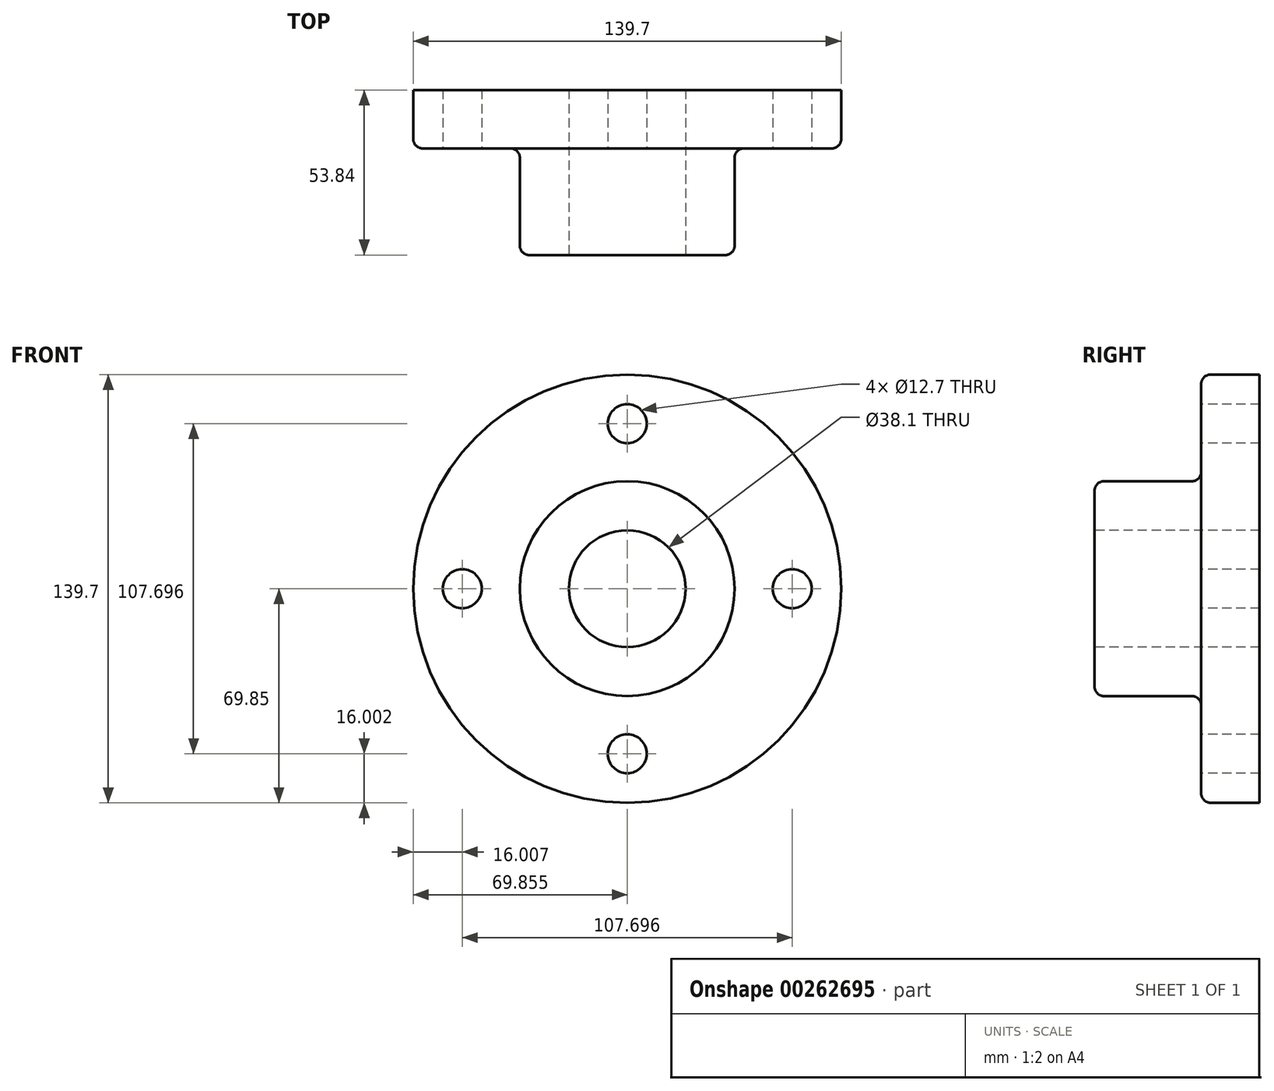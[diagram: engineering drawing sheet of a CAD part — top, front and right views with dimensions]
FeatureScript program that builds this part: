
annotation { "Feature Type Name" : "Feature", "Feature Type Description" : "" }
export const myFeature = defineFeature(function(context is Context, id is Id, definition is map)
    precondition{}
    {
        {
            var Q0;
            Q0=qCreatedBy(makeId("Top.planeOp"),FACE);
            var sketch = newSketch(context, id + "F0", { "sketchPlane" : qUnion([Q0])});
            skLineSegment(sketch, "E0.bottom", {"start": v(-26.3, -57.06) * mm, "end": v(8.75, -57.06) * mm});
            skLineSegment(sketch, "E0.top", {"start": v(-26.3, -3.22) * mm, "end": v(43.54, -3.22) * mm});
            skLineSegment(sketch, "E0.left", {"start": v(-26.3, -57.06) * mm, "end": v(-26.3, -3.22) * mm});
            skLineSegment(sketch, "E0.right", {"start": v(43.54, -22.27) * mm, "end": v(43.54, -3.22) * mm});
            skLineSegment(sketch, "E1.top", {"start": v(43.54, -22.27) * mm, "end": v(8.75, -22.27) * mm});
            skLineSegment(sketch, "E1.right", {"start": v(8.75, -57.06) * mm, "end": v(8.75, -22.27) * mm});
            skSolve(sketch);
        }
        {
            var Q0;
            Q0 = qSketchRegion(id + "F0", true);
            var Q1;
            Q1=sQuery(id+"F0.wireOp",EDGE,"E0.left");
            revolve(context, id + "F1", {"entities" : qUnion([Q0]), "axis" : qUnion([Q1]), "revolveType" : RevolveType.FULL});
        }
        {
            var Q0;
            Q0=makeQuery(id+"F1.opRevolve","SWEPT_FACE",FACE,{"disambiguationData":[OSD([sQuery(id+"F0.wireOp",EDGE,"E1.top")])]});
            var sketch = newSketch(context, id + "F2", { "sketchPlane" : qUnion([Q0])});
            skCircle(sketch, "E2", {"center": v(-26.3, 0) * mm, "radius": 19.05 * mm});
            skSolve(sketch);
        }
        {
            var Q0;
            Q0 = qSketchRegion(id + "F2", true);
            extrude(context, id + "F3", {"entities" : qUnion([Q0]), "operationType" : NewBodyOperationType.REMOVE, "endBound" : BoundingType.SYMMETRIC, "oppositeDirection" : true, "depth" : 101.6 * mm});
        }
        {
            var Q0;
            Q0=makeQuery(id+"F1.opRevolve","SWEPT_FACE",FACE,{"disambiguationData":[OSD([sQuery(id+"F0.wireOp",EDGE,"E1.top")])]});
            var sketch = newSketch(context, id + "F4", { "sketchPlane" : qUnion([Q0])});
            skCircle(sketch, "E3", {"center": v(-80.15, 0) * mm, "radius": 6.35 * mm});
            skCircle(sketch, "E4", {"center": v(27.54, 0) * mm, "radius": 6.35 * mm});
            skCircle(sketch, "E5", {"center": v(-26.3, 53.85) * mm, "radius": 6.35 * mm});
            skCircle(sketch, "E6", {"center": v(-26.3, -53.85) * mm, "radius": 6.35 * mm});
            skPoint(sketch, "E7.center.orphan", {"position": v(-26.3, 0) * mm});
            skSolve(sketch);
        }
        {
            var Q0;
            Q0 = qSketchRegion(id + "F4", true);
            extrude(context, id + "F5", {"entities" : qUnion([Q0]), "operationType" : NewBodyOperationType.REMOVE, "endBound" : BoundingType.SYMMETRIC, "oppositeDirection" : true, "depth" : 101.6 * mm});
        }
        {
            var Q0;
            Q0=makeQuery(id+"F1.opRevolve","SWEPT_EDGE",EDGE,{"disambiguationData":[OSD([sQuery(id+"F0.wireOp",EDGE,"E0.right"),sQuery(id+"F0.wireOp",EDGE,"E1.top")])]});
            var Q1;
            Q1=makeQuery(id+"F1.opRevolve","SWEPT_EDGE",EDGE,{"disambiguationData":[OSD([sQuery(id+"F0.wireOp",EDGE,"E1.top"),sQuery(id+"F0.wireOp",EDGE,"E1.right")])]});
            var Q2;
            Q2=makeQuery(id+"F1.opRevolve","SWEPT_EDGE",EDGE,{"disambiguationData":[OSD([sQuery(id+"F0.wireOp",EDGE,"E0.bottom"),sQuery(id+"F0.wireOp",EDGE,"E1.right")])]});
            fillet(context, id + "F6", {"entities" : qUnion([Q0, Q1, Q2]), "radius" : 3.05 * mm, "tangentPropagation" : true, "allowEdgeOverflow" : false});
        }
    });
